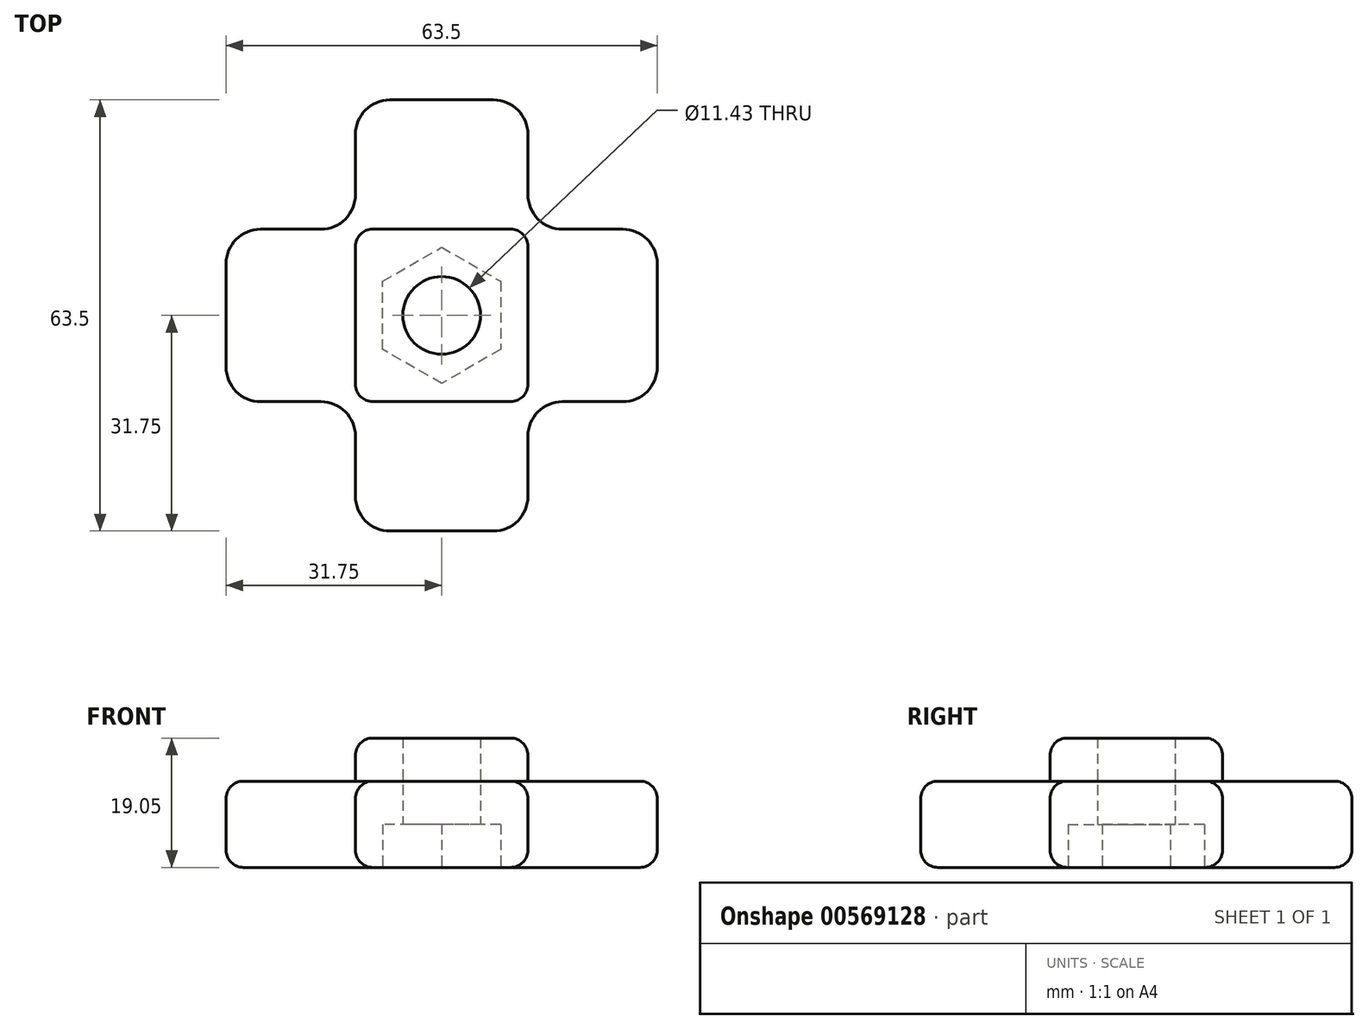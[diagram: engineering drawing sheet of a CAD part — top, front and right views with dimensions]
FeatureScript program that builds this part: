
annotation { "Feature Type Name" : "Feature", "Feature Type Description" : "" }
export const myFeature = defineFeature(function(context is Context, id is Id, definition is map)
    precondition{}
    {
        {
            var Q0;
            Q0=qCreatedBy(makeId("Top.planeOp"),FACE);
            var sketch = newSketch(context, id + "F0", { "sketchPlane" : qUnion([Q0])});
            skCircle(sketch, "E0.cCircle", {"center": v(0, 0) * mm, "radius": 8.69 * mm, "construction": true});
            skLineSegment(sketch, "E0.0", {"start": v(-8.69, -5.02) * mm, "end": v(-8.69, 5.02) * mm});
            skLineSegment(sketch, "E0.1", {"start": v(-8.69, 5.02) * mm, "end": v(0, 10.03) * mm});
            skLineSegment(sketch, "E0.2", {"start": v(0, 10.03) * mm, "end": v(8.69, 5.02) * mm});
            skLineSegment(sketch, "E0.3", {"start": v(8.69, 5.02) * mm, "end": v(8.69, -5.02) * mm});
            skLineSegment(sketch, "E0.4", {"start": v(8.69, -5.02) * mm, "end": v(0, -10.03) * mm});
            skLineSegment(sketch, "E0.5", {"start": v(0, -10.03) * mm, "end": v(-8.69, -5.02) * mm});
            skPoint(sketch, "E0.0.midPoint", {"position": v(-8.69, 0) * mm});
            skLineSegment(sketch, "E1.bottom", {"start": v(-12.7, 12.7) * mm, "end": v(12.7, 12.7) * mm});
            skLineSegment(sketch, "E1.top", {"start": v(-12.7, -12.7) * mm, "end": v(12.7, -12.7) * mm});
            skLineSegment(sketch, "E1.left", {"start": v(-12.7, 12.7) * mm, "end": v(-12.7, -12.7) * mm});
            skLineSegment(sketch, "E1.right", {"start": v(12.7, 12.7) * mm, "end": v(12.7, -12.7) * mm});
            skLineSegment(sketch, "E2.top", {"start": v(-12.7, -31.75) * mm, "end": v(12.7, -31.75) * mm});
            skLineSegment(sketch, "E2.left", {"start": v(-12.7, -12.7) * mm, "end": v(-12.7, -31.75) * mm});
            skLineSegment(sketch, "E2.right", {"start": v(12.7, -12.7) * mm, "end": v(12.7, -31.75) * mm});
            skLineSegment(sketch, "E3.bottom", {"start": v(12.7, 12.7) * mm, "end": v(31.75, 12.7) * mm});
            skLineSegment(sketch, "E3.top", {"start": v(12.7, -12.7) * mm, "end": v(31.75, -12.7) * mm});
            skLineSegment(sketch, "E3.right", {"start": v(31.75, 12.7) * mm, "end": v(31.75, -12.7) * mm});
            skLineSegment(sketch, "E4.top", {"start": v(-12.7, 31.75) * mm, "end": v(12.7, 31.75) * mm});
            skLineSegment(sketch, "E4.left", {"start": v(-12.7, 12.7) * mm, "end": v(-12.7, 31.75) * mm});
            skLineSegment(sketch, "E4.right", {"start": v(12.7, 12.7) * mm, "end": v(12.7, 31.75) * mm});
            skLineSegment(sketch, "E5.bottom", {"start": v(-12.7, 12.7) * mm, "end": v(-31.75, 12.7) * mm});
            skLineSegment(sketch, "E5.top", {"start": v(-12.7, -12.7) * mm, "end": v(-31.75, -12.7) * mm});
            skLineSegment(sketch, "E5.right", {"start": v(-31.75, 12.7) * mm, "end": v(-31.75, -12.7) * mm});
            skCircle(sketch, "E6", {"center": v(0, 0) * mm, "radius": 5.72 * mm});
            skSolve(sketch);
        }
        {
            var Q0;
            Q0=makeQuery(id+"F0.imprint","IMPRINT",FACE,{"disambiguationData":[TD([[makeQuery(id+"F0.imprint","IMPRINT",EDGE,{"derivedFrom":sQuery(id+"F0.wireOp",EDGE,"E3.bottom")}),-1.0]])]});
            var Q1;
            Q1=makeQuery(id+"F0.imprint","IMPRINT",FACE,{"disambiguationData":[TD([[makeQuery(id+"F0.imprint","IMPRINT",EDGE,{"derivedFrom":sQuery(id+"F0.wireOp",EDGE,"E1.bottom")}),1.0]])]});
            var Q2;
            Q2=makeQuery(id+"F0.imprint","IMPRINT",FACE,{"disambiguationData":[TD([[makeQuery(id+"F0.imprint","IMPRINT",EDGE,{"derivedFrom":sQuery(id+"F0.wireOp",EDGE,"E1.top")}),-1.0]])]});
            var Q3;
            Q3=makeQuery(id+"F0.imprint","IMPRINT",FACE,{"disambiguationData":[TD([[makeQuery(id+"F0.imprint","IMPRINT",EDGE,{"derivedFrom":sQuery(id+"F0.wireOp",EDGE,"E0.0")}),1.0]])]});
            var Q4;
            Q4=makeQuery(id+"F0.imprint","IMPRINT",FACE,{"disambiguationData":[TD([[makeQuery(id+"F0.imprint","IMPRINT",EDGE,{"derivedFrom":sQuery(id+"F0.wireOp",EDGE,"E5.bottom")}),1.0]])]});
            extrude(context, id + "F1", {"entities" : qUnion([Q0, Q1, Q2, Q3, Q4]), "depth" : 12.7 * mm, "offsetDistance" : 25.4 * mm});
        }
        {
            var Q0;
            Q0=makeQuery(id+"F0.imprint","IMPRINT",FACE,{"disambiguationData":[TD([[makeQuery(id+"F0.imprint","IMPRINT",EDGE,{"derivedFrom":sQuery(id+"F0.wireOp",EDGE,"E0.0")}),1.0]])]});
            var Q1;
            Q1=makeQuery(id+"F0.imprint","IMPRINT",FACE,{"disambiguationData":[TD([[makeQuery(id+"F0.imprint","IMPRINT",EDGE,{"derivedFrom":sQuery(id+"F0.wireOp",EDGE,"E0.0")}),-1.0]])]});
            extrude(context, id + "F2", {"entities" : qUnion([Q0, Q1]), "operationType" : NewBodyOperationType.ADD, "depth" : 19.05 * mm, "offsetDistance" : 25.4 * mm});
        }
        {
            var Q0;
            Q0=makeQuery(id+"F0.imprint","IMPRINT",FACE,{"disambiguationData":[TD([[makeQuery(id+"F0.imprint","IMPRINT",EDGE,{"derivedFrom":sQuery(id+"F0.wireOp",EDGE,"E0.0")}),-1.0]])]});
            extrude(context, id + "F3", {"entities" : qUnion([Q0]), "operationType" : NewBodyOperationType.REMOVE, "depth" : 6.35 * mm, "offsetDistance" : 25.4 * mm});
        }
        {
            var Q0;
            Q0=makeQuery(id+"F1.opExtrude","SWEPT_EDGE",EDGE,{"disambiguationData":[OSD([sQuery(id+"F0.wireOp",EDGE,"E1.bottom"),sQuery(id+"F0.wireOp",EDGE,"E4.left"),sQuery(id+"F0.wireOp",EDGE,"E5.bottom"),sQuery(id+"F0.wireOp",EDGE,"E1.left")])]});
            var Q1;
            Q1=makeQuery(id+"F1.opExtrude","SWEPT_EDGE",EDGE,{"disambiguationData":[OSD([sQuery(id+"F0.wireOp",EDGE,"E3.bottom"),sQuery(id+"F0.wireOp",EDGE,"E1.right"),sQuery(id+"F0.wireOp",EDGE,"E1.bottom"),sQuery(id+"F0.wireOp",EDGE,"E4.right")])]});
            var Q2;
            Q2=makeQuery(id+"F1.opExtrude","SWEPT_EDGE",EDGE,{"disambiguationData":[OSD([sQuery(id+"F0.wireOp",EDGE,"E1.top"),sQuery(id+"F0.wireOp",EDGE,"E2.right"),sQuery(id+"F0.wireOp",EDGE,"E3.top"),sQuery(id+"F0.wireOp",EDGE,"E1.right")])]});
            var Q3;
            Q3=makeQuery(id+"F1.opExtrude","SWEPT_EDGE",EDGE,{"disambiguationData":[OSD([sQuery(id+"F0.wireOp",EDGE,"E1.top"),sQuery(id+"F0.wireOp",EDGE,"E2.left"),sQuery(id+"F0.wireOp",EDGE,"E5.top"),sQuery(id+"F0.wireOp",EDGE,"E1.left")])]});
            var Q4;
            Q4=makeQuery(id+"F1.opExtrude","SWEPT_EDGE",EDGE,{"disambiguationData":[OSD([sQuery(id+"F0.wireOp",EDGE,"E3.top"),sQuery(id+"F0.wireOp",EDGE,"E3.right")])]});
            var Q5;
            Q5=makeQuery(id+"F1.opExtrude","SWEPT_EDGE",EDGE,{"disambiguationData":[OSD([sQuery(id+"F0.wireOp",EDGE,"E3.bottom"),sQuery(id+"F0.wireOp",EDGE,"E3.right")])]});
            var Q6;
            Q6=makeQuery(id+"F1.opExtrude","SWEPT_EDGE",EDGE,{"disambiguationData":[OSD([sQuery(id+"F0.wireOp",EDGE,"E4.top"),sQuery(id+"F0.wireOp",EDGE,"E4.right")])]});
            var Q7;
            Q7=makeQuery(id+"F1.opExtrude","SWEPT_EDGE",EDGE,{"disambiguationData":[OSD([sQuery(id+"F0.wireOp",EDGE,"E4.top"),sQuery(id+"F0.wireOp",EDGE,"E4.left")])]});
            var Q8;
            Q8=makeQuery(id+"F1.opExtrude","SWEPT_EDGE",EDGE,{"disambiguationData":[OSD([sQuery(id+"F0.wireOp",EDGE,"E5.bottom"),sQuery(id+"F0.wireOp",EDGE,"E5.right")])]});
            var Q9;
            Q9=makeQuery(id+"F1.opExtrude","SWEPT_EDGE",EDGE,{"disambiguationData":[OSD([sQuery(id+"F0.wireOp",EDGE,"E5.top"),sQuery(id+"F0.wireOp",EDGE,"E5.right")])]});
            var Q10;
            Q10=makeQuery(id+"F1.opExtrude","SWEPT_EDGE",EDGE,{"disambiguationData":[OSD([sQuery(id+"F0.wireOp",EDGE,"E2.top"),sQuery(id+"F0.wireOp",EDGE,"E2.left")])]});
            var Q11;
            Q11=makeQuery(id+"F1.opExtrude","SWEPT_EDGE",EDGE,{"disambiguationData":[OSD([sQuery(id+"F0.wireOp",EDGE,"E2.top"),sQuery(id+"F0.wireOp",EDGE,"E2.right")])]});
            fillet(context, id + "F4", {"entities" : qUnion([Q0, Q1, Q2, Q3, Q4, Q5, Q6, Q7, Q8, Q9, Q10, Q11]), "radius" : 5.08 * mm, "tangentPropagation" : true, "allowEdgeOverflow" : false});
        }
        {
            var Q0;
            Q0=makeQuery(id+"F2.opExtrude","CAP_EDGE",EDGE,{"disambiguationData":[OSD([sQuery(id+"F0.wireOp",EDGE,"E1.bottom")])],"isStart":false});
            var Q1;
            Q1=makeQuery(id+"F2.opExtrude","CAP_EDGE",EDGE,{"disambiguationData":[OSD([sQuery(id+"F0.wireOp",EDGE,"E1.left")])],"isStart":false});
            var Q2;
            Q2=makeQuery(id+"F2.opExtrude","CAP_EDGE",EDGE,{"disambiguationData":[OSD([sQuery(id+"F0.wireOp",EDGE,"E1.top")])],"isStart":false});
            var Q3;
            Q3=makeQuery(id+"F2.opExtrude","CAP_EDGE",EDGE,{"disambiguationData":[OSD([sQuery(id+"F0.wireOp",EDGE,"E1.right")])],"isStart":false});
            var Q4;
            Q4=makeQuery(id+"F2.opExtrude","SWEPT_EDGE",EDGE,{"disambiguationData":[OSD([sQuery(id+"F0.wireOp",EDGE,"E1.top"),sQuery(id+"F0.wireOp",EDGE,"E2.right"),sQuery(id+"F0.wireOp",EDGE,"E3.top"),sQuery(id+"F0.wireOp",EDGE,"E1.right")])]});
            var Q5;
            Q5=makeQuery(id+"F2.opExtrude","SWEPT_EDGE",EDGE,{"disambiguationData":[OSD([sQuery(id+"F0.wireOp",EDGE,"E3.bottom"),sQuery(id+"F0.wireOp",EDGE,"E1.right"),sQuery(id+"F0.wireOp",EDGE,"E1.bottom"),sQuery(id+"F0.wireOp",EDGE,"E4.right")])]});
            var Q6;
            Q6=makeQuery(id+"F2.opExtrude","SWEPT_EDGE",EDGE,{"disambiguationData":[OSD([sQuery(id+"F0.wireOp",EDGE,"E1.bottom"),sQuery(id+"F0.wireOp",EDGE,"E4.left"),sQuery(id+"F0.wireOp",EDGE,"E5.bottom"),sQuery(id+"F0.wireOp",EDGE,"E1.left")])]});
            var Q7;
            Q7=makeQuery(id+"F2.opExtrude","SWEPT_EDGE",EDGE,{"disambiguationData":[OSD([sQuery(id+"F0.wireOp",EDGE,"E1.top"),sQuery(id+"F0.wireOp",EDGE,"E2.left"),sQuery(id+"F0.wireOp",EDGE,"E5.top"),sQuery(id+"F0.wireOp",EDGE,"E1.left")])]});
            fillet(context, id + "F5", {"entities" : qUnion([Q0, Q1, Q2, Q3, Q4, Q5, Q6, Q7]), "radius" : 2.54 * mm, "tangentPropagation" : true, "allowEdgeOverflow" : false});
        }
        {
            var Q0;
            Q0=makeQuery(id+"F1.opExtrude","CAP_EDGE",EDGE,{"disambiguationData":[OSD([sQuery(id+"F0.wireOp",EDGE,"E3.right")])],"isStart":true});
            var Q1;
            Q1=makeQuery(id+"F1.opExtrude","CAP_EDGE",EDGE,{"disambiguationData":[OSD([sQuery(id+"F0.wireOp",EDGE,"E3.right")])],"isStart":false});
            fillet(context, id + "F6", {"entities" : qUnion([Q0, Q1]), "radius" : 2.54 * mm, "tangentPropagation" : true, "allowEdgeOverflow" : false});
        }
    });
